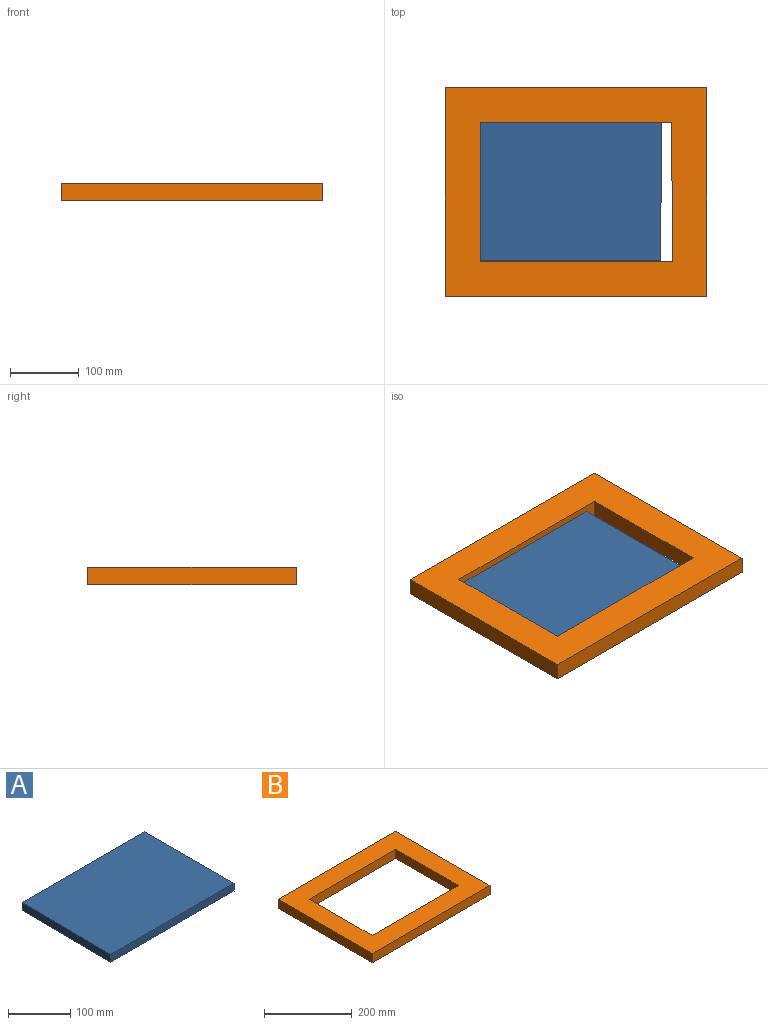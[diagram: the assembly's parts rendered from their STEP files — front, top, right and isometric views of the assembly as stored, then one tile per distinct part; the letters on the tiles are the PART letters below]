
ASSEMBLY  parts=2 mates=2
PART A: 6 faces, bbox 280x202.6x15.2 mm
  f0: plane 202.57x15.24mm, normal (-1,0.01,0), area 3087.3mm2, adj f1,f3,f4,f5
  f1: plane 280.01x15.24mm, normal (0,-1,0), area 4267.4mm2, adj f0,f2,f4,f5
  f2: plane 202.57x15.24mm, normal (1,0,0), area 3087.2mm2, adj f1,f3,f4,f5
  f3: plane 278.31x15.24mm, normal (0,1,0), area 4241.5mm2, adj f0,f2,f4,f5
  f4: plane 280.01x202.57mm, normal (0,0,-1), area 56551.4mm2, adj f0,f1,f2,f3
  f5: plane 280.01x202.57mm, normal (0,0,1), area 56551.4mm2, adj f0,f1,f2,f3
PART B: 10 faces, bbox 381x304.3x25.4 mm
  f0: plane 381x25.4mm, normal (0,1,0), area 9677.4mm2, adj f1,f7,f8,f9
  f1: plane 304.27x25.4mm, normal (-1,0,0), area 7728.4mm2, adj f0,f2,f8,f9
  f2: plane 381x25.4mm, normal (0,-1,0), area 9677.4mm2, adj f1,f7,f8,f9
  f3: plane 280.37x25.4mm, normal (0,1,0), area 7121.5mm2, adj f4,f6,f8,f9
  f4: plane 203.31x25.4mm, normal (1,0,0), area 5164mm2, adj f3,f5,f8,f9
  f5: plane 279.35x25.4mm, normal (0,-1,0), area 7095.5mm2, adj f4,f6,f8,f9
  f6: plane 203.29x25.4mm, normal (-1,0,0), area 5163.6mm2, adj f3,f5,f8,f9
  f7: plane 304.27x25.4mm, normal (1,0,0), area 7728.4mm2, adj f0,f2,f8,f9
  f8: plane 381x304.27mm, normal (0,0,-1), area 59030mm2, adj f0,f1,f2,f3,f4,f5,f6,f7
  f9: plane 381x304.27mm, normal (0,0,1), area 59030mm2, adj f0,f1,f2,f3,f4,f5,f6,f7
PLACE A rot(axis=(0,0,-1),0deg) t=(-98.2,-155.77,214.42)mm
PLACE B t=(-83.59,-155.87,224.58)mm fixed
MATE planar A.f3 <-> B.f5  axis (0,1,0) through (-188.18,-235.2,206.8)mm
MATE planar A.f4 <-> B.f8  axis (0,0,-1) through (-188.65,-336.59,199.18)mm
